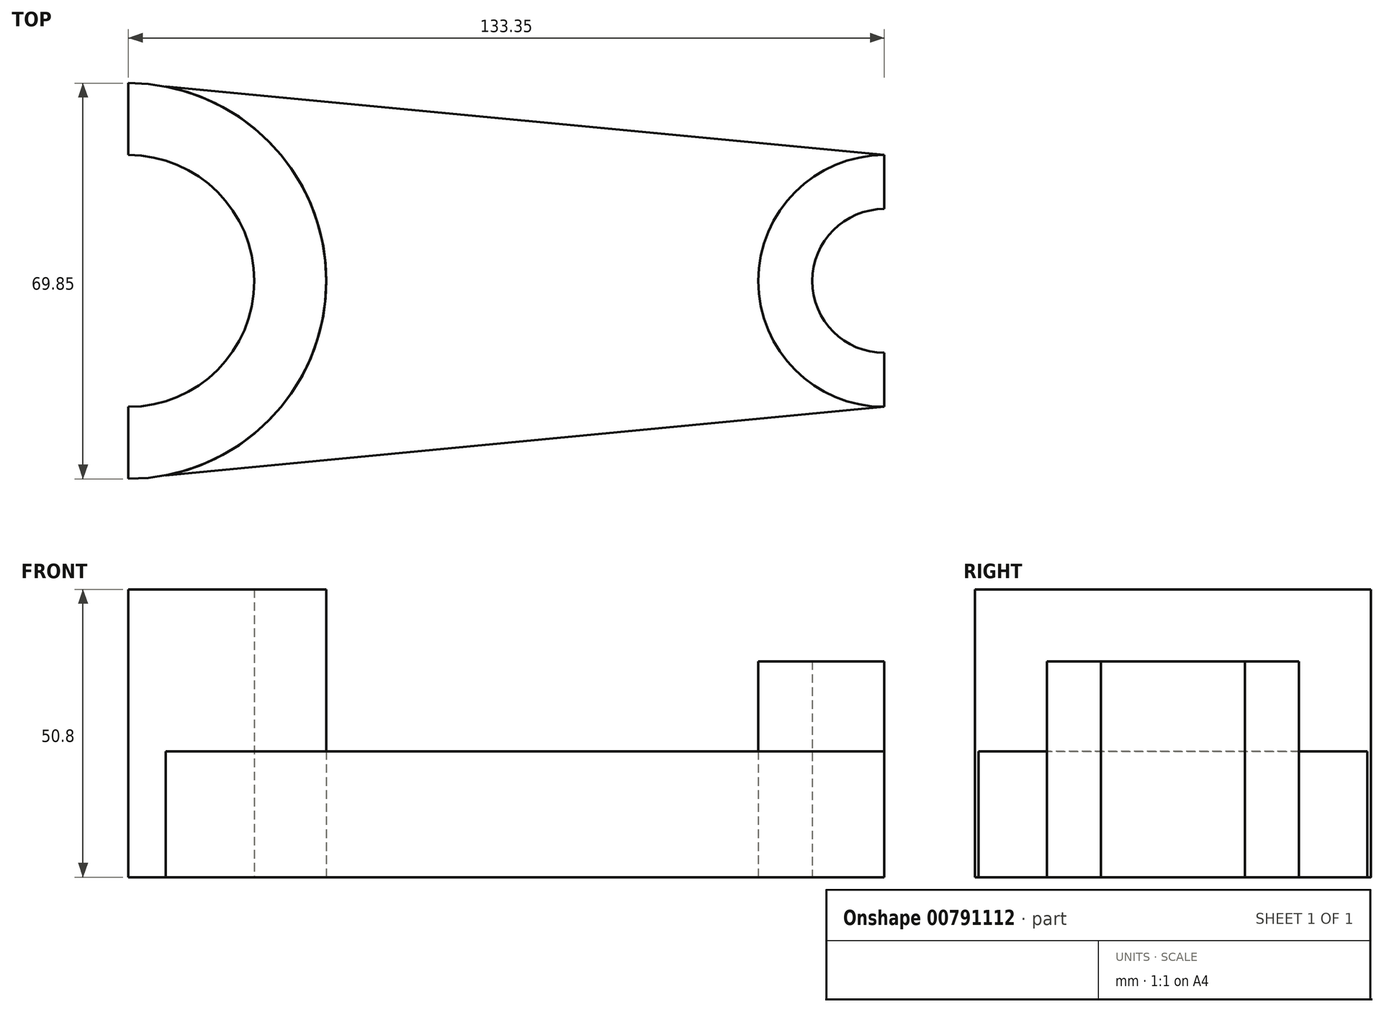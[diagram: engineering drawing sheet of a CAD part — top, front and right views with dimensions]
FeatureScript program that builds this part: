
annotation { "Feature Type Name" : "Feature", "Feature Type Description" : "" }
export const myFeature = defineFeature(function(context is Context, id is Id, definition is map)
    precondition{}
    {
        {
            var Q0;
            Q0=qCreatedBy(makeId("Top.planeOp"),FACE);
            var sketch = newSketch(context, id + "F0", { "sketchPlane" : qUnion([Q0])});
            skCircle(sketch, "E0", {"center": v(0, 0) * mm, "radius": 34.93 * mm});
            skLineSegment(sketch, "E1", {"start": v(0, 0) * mm, "end": v(133.35, 0) * mm});
            skCircle(sketch, "E2", {"center": v(133.35, 0) * mm, "radius": 22.23 * mm});
            skLineSegment(sketch, "E3", {"start": v(133.35, 0) * mm, "end": v(133.35, 22.23) * mm});
            skLineSegment(sketch, "E4", {"start": v(133.35, 22.23) * mm, "end": v(133.35, -22.23) * mm});
            skLineSegment(sketch, "E5", {"start": v(0, 0) * mm, "end": v(0, 34.93) * mm});
            skLineSegment(sketch, "E6", {"start": v(0, 34.93) * mm, "end": v(0, -34.93) * mm});
            skCircle(sketch, "E7", {"center": v(0, 0) * mm, "radius": 22.23 * mm});
            skCircle(sketch, "E8", {"center": v(133.35, 0) * mm, "radius": 12.7 * mm});
            skLineSegment(sketch, "E9", {"start": v(133.35, -22.23) * mm, "end": v(0, -34.93) * mm});
            skLineSegment(sketch, "E10", {"start": v(133.35, 22.23) * mm, "end": v(0, 34.93) * mm});
            skSolve(sketch);
        }
        {
            var Q0;
            {var subQ0=sQuery(id+"F0.wireOp",EDGE,"0njxot8u-2kJx-1oq4-rhc0-frSpkdHslES9");var subQ2=sQuery(id+"F0.wireOp",EDGE,"E0");var subQ6=makeQuery(id+"F0.imprint","INTERSECT",VERTEX,{"derivedFrom":[subQ2,subQ0]});Q0=makeQuery(id+"F0.imprint","IMPRINT",FACE,{"disambiguationData":[TD([[makeQuery(id+"F0.imprint","IMPRINT",EDGE,{"disambiguationData":[TD([[subQ6,-1.0]])],"derivedFrom":subQ2}),1.0]])]});}
            var Q1;
            {var subQ0=sQuery(id+"F0.wireOp",EDGE,"Wao20cou-xmM5-zHhU-0WHO-NzNt5jBPWN5H");var subQ2=sQuery(id+"F0.wireOp",EDGE,"E0");var subQ4=makeQuery(id+"F0.imprint","INTERSECT",VERTEX,{"derivedFrom":[subQ2,subQ0]});Q1=makeQuery(id+"F0.imprint","IMPRINT",FACE,{"disambiguationData":[TD([[makeQuery(id+"F0.imprint","IMPRINT",EDGE,{"disambiguationData":[TD([[subQ4,1.0]])],"derivedFrom":subQ2}),1.0]])]});}
            var Q2;
            {var subQ0=sQuery(id+"F0.wireOp",EDGE,"E6");var subQ4=sQuery(id+"F0.wireOp",EDGE,"E7");var subQ5=makeQuery(id+"F0.imprint","INTERSECT",VERTEX,{"disambiguationData":[OD(0.0)],"derivedFrom":[subQ0,subQ4]});Q2=makeQuery(id+"F0.imprint","IMPRINT",FACE,{"disambiguationData":[TD([[makeQuery(id+"F0.imprint","IMPRINT",EDGE,{"disambiguationData":[TD([[subQ5,-1.0]])],"derivedFrom":subQ4}),-1.0]])]});}
            var Q3;
            {var subQ0=sQuery(id+"F0.wireOp",EDGE,"E10");var subQ2=sQuery(id+"F0.wireOp",EDGE,"E0");var subQ9=makeQuery(id+"F0.imprint","INTERSECT",VERTEX,{"derivedFrom":[subQ2,subQ0]});Q3=makeQuery(id+"F0.imprint","IMPRINT",FACE,{"disambiguationData":[TD([[makeQuery(id+"F0.imprint","IMPRINT",EDGE,{"disambiguationData":[TD([[subQ9,1.0]])],"derivedFrom":subQ2}),1.0]])]});}
            var Q4;
            {var subQ5=sQuery(id+"F0.wireOp",EDGE,"E9");var subQ6=sQuery(id+"F0.wireOp",EDGE,"E0");var subQ9=makeQuery(id+"F0.imprint","INTERSECT",VERTEX,{"derivedFrom":[subQ6,subQ5]});Q4=makeQuery(id+"F0.imprint","IMPRINT",FACE,{"disambiguationData":[TD([[makeQuery(id+"F0.imprint","IMPRINT",EDGE,{"disambiguationData":[TD([[subQ9,-1.0]])],"derivedFrom":subQ6}),1.0]])]});}
            extrude(context, id + "F1", {"entities" : qUnion([Q0, Q1, Q2, Q3, Q4]), "depth" : 50.8 * mm, "offsetDistance" : 25.4 * mm});
        }
        {
            var Q0;
            {var subQ0=sQuery(id+"F0.wireOp",EDGE,"E2");var subQ1=sQuery(id+"F0.wireOp",EDGE,"E1");var subQ2=makeQuery(id+"F0.imprint","INTERSECT",VERTEX,{"derivedFrom":[subQ1,subQ0]});Q0=makeQuery(id+"F0.imprint","IMPRINT",FACE,{"disambiguationData":[TD([[makeQuery(id+"F0.imprint","IMPRINT",EDGE,{"disambiguationData":[TD([[subQ2,-1.0]])],"derivedFrom":subQ1}),-1.0]])]});}
            var Q1;
            {var subQ0=sQuery(id+"F0.wireOp",EDGE,"E4");var subQ4=sQuery(id+"F0.wireOp",EDGE,"E8");var subQ5=makeQuery(id+"F0.imprint","INTERSECT",VERTEX,{"disambiguationData":[OD(0.0)],"derivedFrom":[subQ0,subQ4]});Q1=makeQuery(id+"F0.imprint","IMPRINT",FACE,{"disambiguationData":[TD([[makeQuery(id+"F0.imprint","IMPRINT",EDGE,{"disambiguationData":[TD([[subQ5,1.0]])],"derivedFrom":subQ4}),-1.0]])]});}
            var Q2;
            {var subQ0=sQuery(id+"F0.wireOp",EDGE,"E2");var subQ1=sQuery(id+"F0.wireOp",EDGE,"E1");var subQ2=makeQuery(id+"F0.imprint","INTERSECT",VERTEX,{"derivedFrom":[subQ1,subQ0]});Q2=makeQuery(id+"F0.imprint","IMPRINT",FACE,{"disambiguationData":[TD([[makeQuery(id+"F0.imprint","IMPRINT",EDGE,{"disambiguationData":[TD([[subQ2,-1.0]])],"derivedFrom":subQ1}),1.0]])]});}
            extrude(context, id + "F2", {"entities" : qUnion([Q0, Q1, Q2]), "depth" : 38.1 * mm, "offsetDistance" : 25.4 * mm});
        }
        {
            var Q0;
            {var subQ0=sQuery(id+"F0.wireOp",EDGE,"0njxot8u-2kJx-1oq4-rhc0-frSpkdHslES9");var subQ1=sQuery(id+"F0.wireOp",EDGE,"E0");var subQ2=makeQuery(id+"F0.imprint","INTERSECT",VERTEX,{"derivedFrom":[subQ1,subQ0]});Q0=makeQuery(id+"F0.imprint","IMPRINT",FACE,{"disambiguationData":[TD([[makeQuery(id+"F0.imprint","IMPRINT",EDGE,{"disambiguationData":[TD([[subQ2,-1.0]])],"derivedFrom":subQ1}),-1.0]])]});}
            var Q1;
            {var subQ0=sQuery(id+"F0.wireOp",EDGE,"Wao20cou-xmM5-zHhU-0WHO-NzNt5jBPWN5H");var subQ1=sQuery(id+"F0.wireOp",EDGE,"E0");var subQ2=makeQuery(id+"F0.imprint","INTERSECT",VERTEX,{"derivedFrom":[subQ1,subQ0]});Q1=makeQuery(id+"F0.imprint","IMPRINT",FACE,{"disambiguationData":[TD([[makeQuery(id+"F0.imprint","IMPRINT",EDGE,{"disambiguationData":[TD([[subQ2,1.0]])],"derivedFrom":subQ1}),-1.0]])]});}
            extrude(context, id + "F3", {"entities" : qUnion([Q0, Q1]), "depth" : 22.22 * mm, "offsetDistance" : 25.4 * mm});
        }
    });
